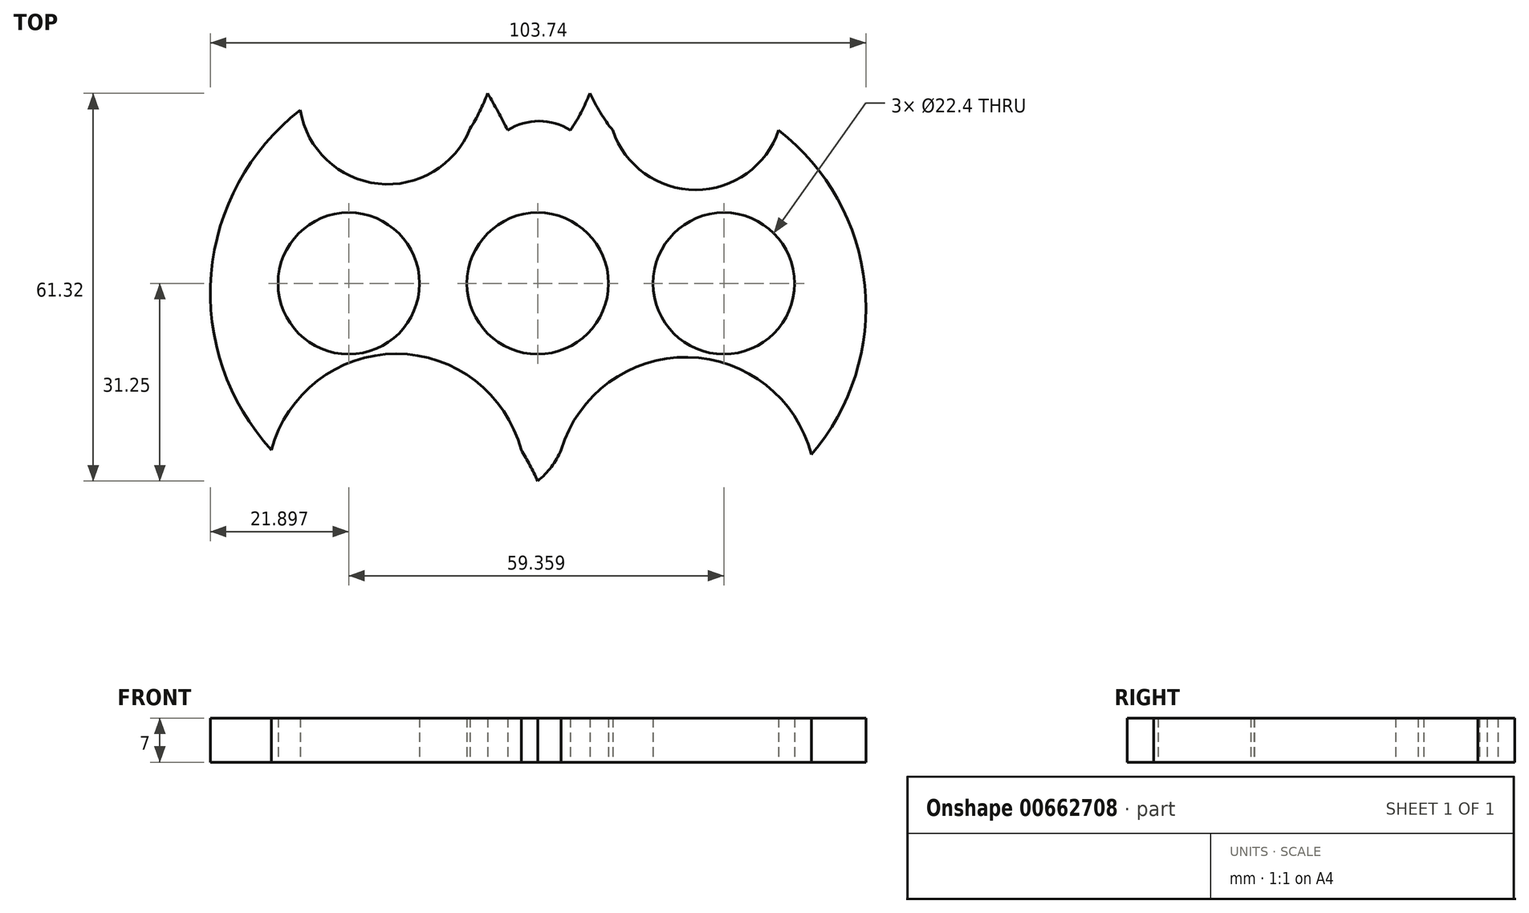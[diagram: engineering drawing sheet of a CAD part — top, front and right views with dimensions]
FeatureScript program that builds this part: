
annotation { "Feature Type Name" : "Feature", "Feature Type Description" : "" }
export const myFeature = defineFeature(function(context is Context, id is Id, definition is map)
    precondition{}
    {
        {
            var Q0;
            Q0=qCreatedBy(makeId("Top.planeOp"),FACE);
            var sketch = newSketch(context, id + "F0", { "sketchPlane" : qUnion([Q0])});
            skCircle(sketch, "E0", {"center": v(0, 0) * mm, "radius": 11.2 * mm});
            skCircle(sketch, "E1", {"center": v(29.46, 0) * mm, "radius": 11.2 * mm});
            skCircle(sketch, "E2", {"center": v(-29.9, 0) * mm, "radius": 11.2 * mm});
            skArc(sketch, "E3", {"start": v(5.18, 24.22) * mm, "mid": v(0.2, 25.68) * mm, "end": v(-4.77, 24.23) * mm});
            skArc(sketch, "E4", {"start": v(-4.77, 24.23) * mm, "mid": v(-6.3, 27.18) * mm, "end": v(-7.92, 30.07) * mm});
            skArc(sketch, "E5", {"start": v(5.18, 24.22) * mm, "mid": v(6.87, 27.06) * mm, "end": v(8.24, 30.07) * mm});
            skArc(sketch, "E6", {"start": v(8.24, 30.07) * mm, "mid": v(9.9, 27.05) * mm, "end": v(11.87, 24.22) * mm});
            skArc(sketch, "E7", {"start": v(-10.7, 24.48) * mm, "mid": v(-9.19, 27.21) * mm, "end": v(-7.92, 30.07) * mm});
            skPoint(sketch, "E8.end.orphan", {"position": v(7.57, -26.34) * mm});
            skArc(sketch, "E9", {"start": v(-2.62, -26.34) * mm, "mid": v(-22.37, -11.14) * mm, "end": v(-42.13, -26.34) * mm});
            skArc(sketch, "E10", {"start": v(43.3, -27.08) * mm, "mid": v(23.79, -11.68) * mm, "end": v(3.72, -26.34) * mm});
            skArc(sketch, "E11", {"start": v(0, -31.25) * mm, "mid": v(-1.24, -28.76) * mm, "end": v(-2.62, -26.34) * mm});
            skArc(sketch, "E12", {"start": v(0, -31.25) * mm, "mid": v(2.16, -29.02) * mm, "end": v(3.72, -26.34) * mm});
            skArc(sketch, "E13", {"start": v(-37.59, 27.4) * mm, "mid": v(-25.25, 15.78) * mm, "end": v(-10.7, 24.48) * mm});
            skArc(sketch, "E14", {"start": v(-37.59, 27.4) * mm, "mid": v(-51.67, 1.53) * mm, "end": v(-42.13, -26.34) * mm});
            skArc(sketch, "E15", {"start": v(11.87, 24.22) * mm, "mid": v(25, 14.8) * mm, "end": v(38.14, 24.22) * mm});
            skArc(sketch, "E16", {"start": v(43.3, -27.08) * mm, "mid": v(51.76, -0.32) * mm, "end": v(38.14, 24.22) * mm});
            skSolve(sketch);
        }
        {
            var Q0;
            Q0=makeQuery(id+"F0.imprint","IMPRINT",FACE,{"disambiguationData":[TD([[makeQuery(id+"F0.imprint","IMPRINT",EDGE,{"derivedFrom":sQuery(id+"F0.wireOp",EDGE,"E0")}),-1.0]])]});
            extrude(context, id + "F1", {"entities" : qUnion([Q0]), "depth" : 7 * mm, "offsetDistance" : 25 * mm});
        }
    });
